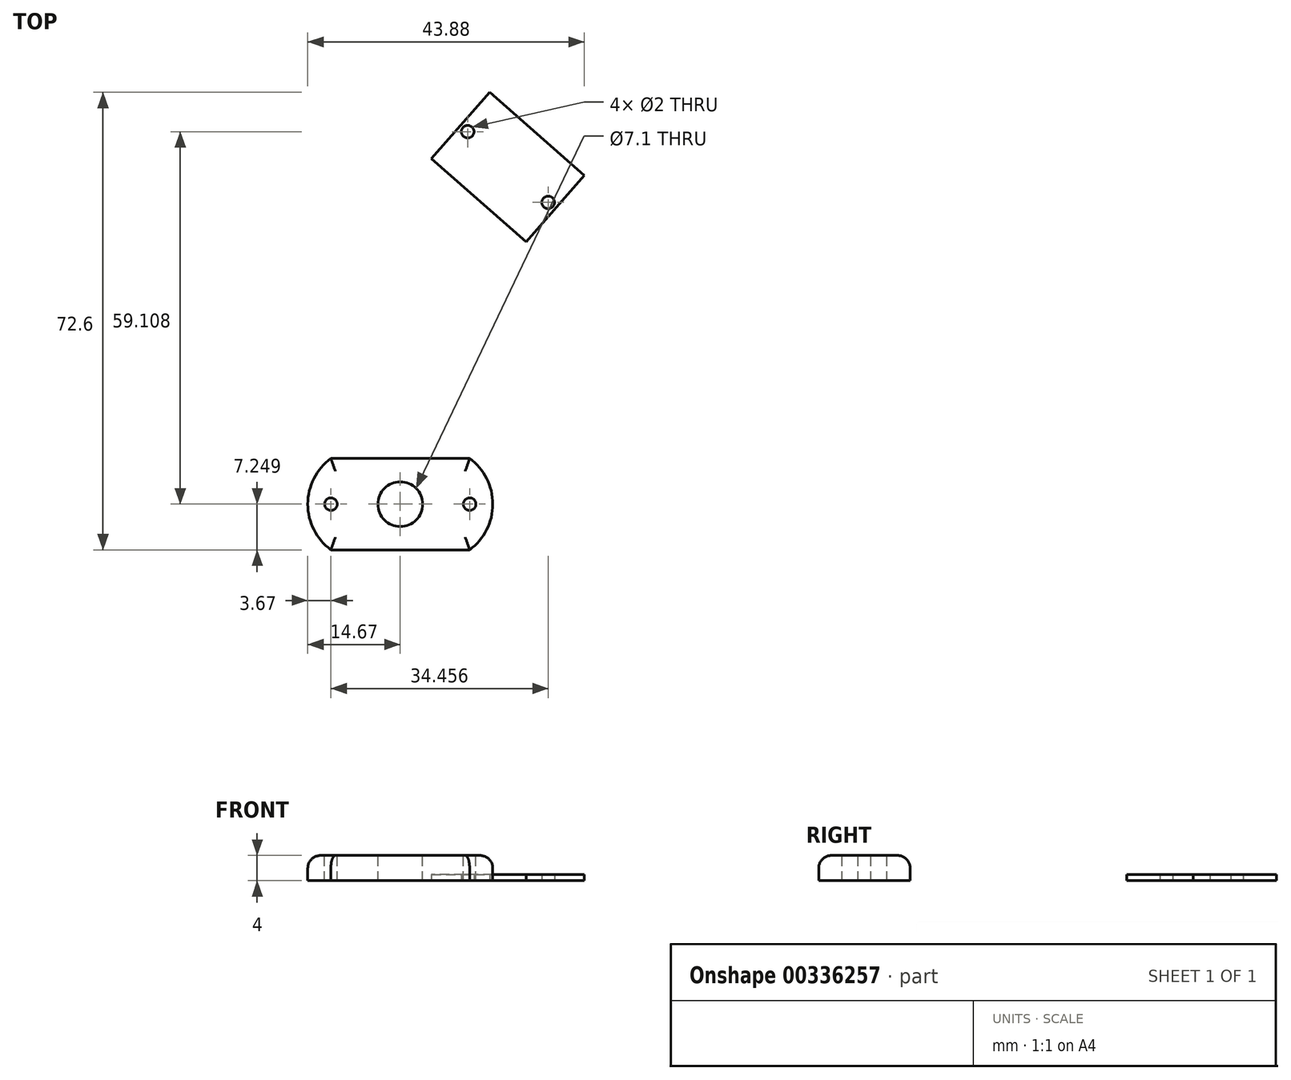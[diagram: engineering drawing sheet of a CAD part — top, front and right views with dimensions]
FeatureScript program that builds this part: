
annotation { "Feature Type Name" : "Feature", "Feature Type Description" : "" }
export const myFeature = defineFeature(function(context is Context, id is Id, definition is map)
    precondition{}
    {
        {
            var Q0;
            Q0=qCreatedBy(makeId("Top.planeOp"),FACE);
            var sketch = newSketch(context, id + "F0", { "sketchPlane" : qUnion([Q0])});
            skLineSegment(sketch, "E0", {"start": v(-28.84, 19) * mm, "end": v(-19.08, 10.41) * mm, "construction": true});
            skLineSegment(sketch, "E1", {"start": v(-19.08, 10.41) * mm, "end": v(-27, 1.4) * mm, "construction": true});
            skLineSegment(sketch, "E2", {"start": v(-27, 1.4) * mm, "end": v(-36.77, 10) * mm, "construction": true});
            skLineSegment(sketch, "E3", {"start": v(-36.77, 10) * mm, "end": v(-28.84, 19) * mm, "construction": true});
            skCircle(sketch, "E4", {"center": v(-34.3, 15.82) * mm, "radius": 1 * mm});
            skCircle(sketch, "E5", {"center": v(-21.54, 4.59) * mm, "radius": 1 * mm});
            skLineSegment(sketch, "E6", {"start": v(-28.77, 25.58) * mm, "end": v(-2.97, 2.87) * mm, "construction": true});
            skLineSegment(sketch, "E7", {"start": v(-30.8, 22.06) * mm, "end": v(-15.8, 8.85) * mm});
            skLineSegment(sketch, "E8", {"start": v(-15.8, 8.85) * mm, "end": v(-25.04, -1.66) * mm});
            skLineSegment(sketch, "E9", {"start": v(-25.04, -1.66) * mm, "end": v(-40.06, 11.55) * mm});
            skLineSegment(sketch, "E10", {"start": v(-40.06, 11.55) * mm, "end": v(-30.8, 22.06) * mm});
            skSolve(sketch);
        }
        {
            var Q0;
            Q0 = qSketchRegion(id + "F0", true);
            extrude(context, id + "F1", {"entities" : qUnion([Q0]), "depth" : 1 * mm});
        }
        {
            var Q0;
            Q0=qCreatedBy(makeId("Top.planeOp"),FACE);
            var sketch = newSketch(context, id + "F2", { "sketchPlane" : qUnion([Q0])});
            skLineSegment(sketch, "E11.top", {"start": v(-34, -36.04) * mm, "end": v(-56, -36.04) * mm});
            skLineSegment(sketch, "E11.left", {"start": v(-34, -50.54) * mm, "end": v(-34, -36.04) * mm});
            skLineSegment(sketch, "E11.right", {"start": v(-56, -50.54) * mm, "end": v(-56, -36.04) * mm});
            skPoint(sketch, "E11.middle", {"position": v(-45, -43.3) * mm});
            skArc(sketch, "E12", {"start": v(-34, -50.54) * mm, "mid": v(-30.33, -43.3) * mm, "end": v(-34, -36.04) * mm});
            skArc(sketch, "E13", {"start": v(-56, -36.04) * mm, "mid": v(-59.67, -43.3) * mm, "end": v(-56, -50.54) * mm});
            skLineSegment(sketch, "E14", {"start": v(-56, -50.54) * mm, "end": v(-34, -50.54) * mm});
            skSolve(sketch);
        }
        {
            var Q0;
            Q0 = qSketchRegion(id + "F2", true);
            extrude(context, id + "F3", {"entities" : qUnion([Q0]), "depth" : 4 * mm});
        }
        {
            var Q0;
            Q0=makeQuery(id+"F3.opExtrude","CAP_FACE",FACE,{"disambiguationData":[OSD([sQuery(id+"F2.wireOp",EDGE,"E11.bottom"),sQuery(id+"F2.wireOp",EDGE,"E11.top"),sQuery(id+"F2.wireOp",EDGE,"E11.left"),sQuery(id+"F2.wireOp",EDGE,"E11.right")])],"isStart":false});
            var sketch = newSketch(context, id + "F4", { "sketchPlane" : qUnion([Q0])});
            skCircle(sketch, "E15", {"center": v(-56, -43.3) * mm, "radius": 1 * mm});
            skCircle(sketch, "E16", {"center": v(-34, -43.3) * mm, "radius": 1 * mm});
            skCircle(sketch, "E17", {"center": v(-45, -43.3) * mm, "radius": 3.55 * mm});
            skSolve(sketch);
        }
        {
            var Q0;
            Q0 = qSketchRegion(id + "F4", true);
            extrude(context, id + "F5", {"entities" : qUnion([Q0]), "operationType" : NewBodyOperationType.REMOVE, "oppositeDirection" : true, "depth" : 5 * mm});
        }
        {
            var Q0;
            Q0=makeQuery(id+"F3.opExtrude","CAP_EDGE",EDGE,{"disambiguationData":[OSD([sQuery(id+"F2.wireOp",EDGE,"E14")])],"isStart":false});
            var Q1;
            Q1=makeQuery(id+"F3.opExtrude","CAP_EDGE",EDGE,{"disambiguationData":[OSD([sQuery(id+"F2.wireOp",EDGE,"E13")])],"isStart":false});
            var Q2;
            Q2=makeQuery(id+"F3.opExtrude","CAP_EDGE",EDGE,{"disambiguationData":[OSD([sQuery(id+"F2.wireOp",EDGE,"E11.top")])],"isStart":false});
            var Q3;
            Q3=makeQuery(id+"F3.opExtrude","CAP_EDGE",EDGE,{"disambiguationData":[OSD([sQuery(id+"F2.wireOp",EDGE,"E12")])],"isStart":false});
            fillet(context, id + "F6", {"entities" : qUnion([Q0, Q1, Q2, Q3]), "radius" : 2 * mm, "tangentPropagation" : true, "allowEdgeOverflow" : false});
        }
    });
